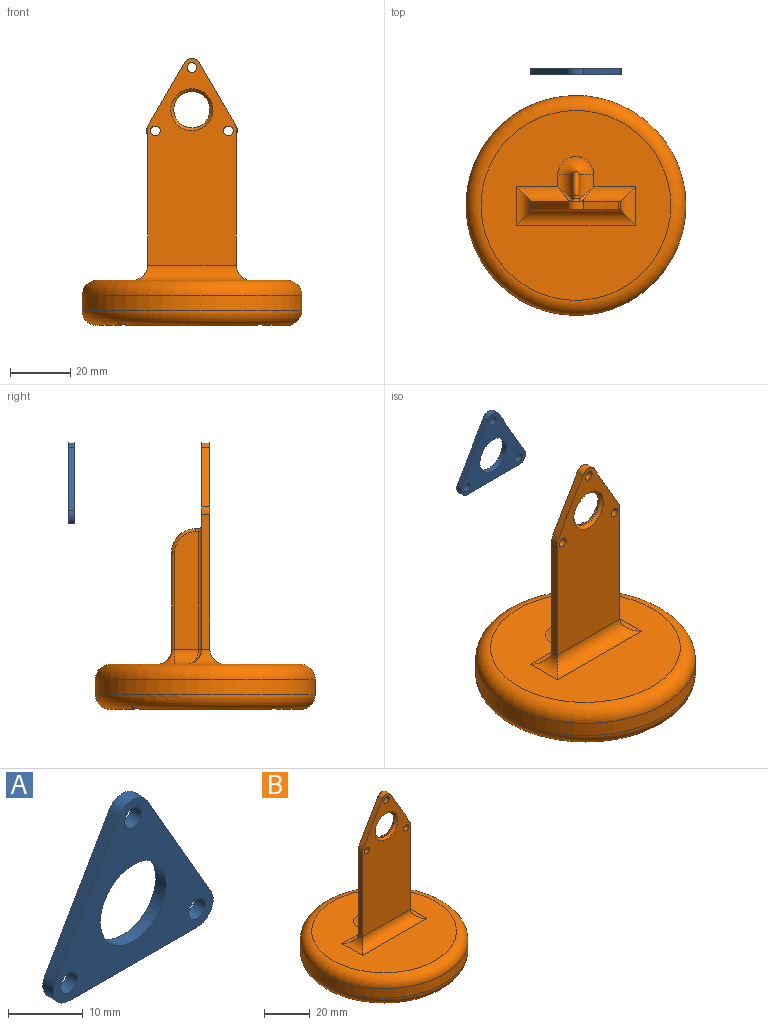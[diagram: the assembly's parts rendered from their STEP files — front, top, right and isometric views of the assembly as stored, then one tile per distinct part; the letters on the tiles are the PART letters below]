
ASSEMBLY  parts=2 mates=1
PART A: 12 faces, bbox 30.2x2x27 mm
  f0: cylinder r=3mm len=4.5mm, axis (0,1,0), area 12.6mm2, adj f1,f9,f10,f11
  f1: plane 21x12.12mm, normal (0.87,0,0.5), area 48.5mm2, adj f0,f2,f10,f11
  f2: cylinder r=3mm len=5.2mm, axis (0,1,0), area 12.6mm2, adj f1,f3,f10,f11
  f3: plane 21x12.12mm, normal (-0.87,0,0.5), area 48.5mm2, adj f2,f4,f10,f11
  f4: cylinder r=3mm len=4.5mm, axis (0,1,0), area 12.6mm2, adj f3,f9,f10,f11
  f5: cylinder r=1.6mm len=3.2mm, axis (0,1,0), area 20.1mm2, adj f10,f11
  f6: cylinder r=1.6mm len=3.2mm, axis (0,1,0), area 20.1mm2, adj f10,f11
  f7: cylinder r=1.6mm len=3.2mm, axis (0,1,0), area 20.1mm2, adj f10,f11
  f8: cylinder r=6.25mm len=12.5mm, axis (0,1,0), area 78.5mm2, adj f10,f11
  f9: plane 24.25x2mm, normal (0,0,-1), area 48.5mm2, adj f0,f4,f10,f11
  f10: plane 30.25x27mm, normal (0,-1,0), area 354.3mm2, adj f0,f1,f2,f3,f4,f5,f6,f7
  f11: plane 30.25x27mm, normal (0,1,0), area 354.3mm2, adj f0,f1,f2,f3,f4,f5,f6,f7
PART B: 62 faces, bbox 79x79x88.7 mm
  f0: plane 40.8x7.5mm, normal (0,0,-1), area 209.4mm2, adj f48,f54
  f1: plane 40.8x7.5mm, normal (0,0,-1), area 209.4mm2, adj f48,f51
  f2: plane 40.8x7.5mm, normal (0,0,-1), area 209.4mm2, adj f48,f57
  f3: plane 63x63mm, normal (0,0,1), area 2511.7mm2, adj f39,f40,f41,f42,f43,f44,f46,f47
  f4: plane 40.8x7.5mm, normal (0,0,-1), area 209.4mm2, adj f48,f60
  f5: cylinder r=36.5mm len=73mm, axis (0,0,-1), area 1146.7mm2, adj f48,f49
  f6: plane 46x11mm, normal (-1,0,0), area 505.3mm2, adj f7,f9,f10,f55,f57,f59
  f7: plane 46x11mm, normal (0,1,0), area 505.3mm2, adj f6,f8,f10,f58,f60,f61
  f8: plane 46x11mm, normal (1,0,0), area 505.3mm2, adj f7,f9,f10,f52,f54,f56
  f9: plane 46x11mm, normal (0,-1,0), area 505.3mm2, adj f6,f8,f10,f50,f51,f53
  f10: plane 46x46mm, normal (0,0,-1), area 2116mm2, adj f6,f7,f8,f9
  f11: plane 19.84x11.45mm, normal (-0.87,0,0.5), area 61.9mm2, adj f12,f20,f21,f22
  f12: cylinder r=5mm len=2.7mm, axis (0,1,0), area 7.1mm2, adj f11,f13,f21,f22
  f13: plane 44.75x2.7mm, normal (-1,0,0), area 120.8mm2, adj f12,f21,f22,f42
  f14: plane 44.75x2.7mm, normal (1,0,0), area 120.8mm2, adj f15,f21,f22,f46
  f15: cylinder r=5mm len=2.7mm, axis (0,1,0), area 7.1mm2, adj f14,f16,f21,f22
  f16: plane 19.84x11.45mm, normal (0.87,0,0.5), area 61.9mm2, adj f15,f20,f21,f22
  f17: cylinder r=1.6mm len=3.2mm, axis (0,1,0), area 27.1mm2, adj f21,f22
  f18: cylinder r=1.6mm len=3.2mm, axis (0,1,0), area 27.1mm2, adj f21,f22
  f19: cylinder r=1.6mm len=3.2mm, axis (0,1,0), area 27.1mm2, adj f21,f22
  f20: cylinder r=3mm len=5.2mm, axis (0,1,0), area 17mm2, adj f11,f16,f21,f22
  f21: plane 68.59x29.45mm, normal (0,-1,0), area 1548mm2, adj f11,f12,f13,f14,f15,f16,f17,f18
  f22: plane 68.59x29.45mm, normal (0,1,0), area 1381.6mm2, adj f11,f12,f13,f14,f15,f16,f17,f18
  f23: cylinder r=0.9mm len=1.8mm, axis (0,-1,0), area 3.3mm2, adj f22,f24,f26,f27
  f24: cylinder r=7.15mm len=14.19mm, axis (0,-1,0), area 24.8mm2, adj f22,f23,f25,f27
  f25: cylinder r=0.9mm len=1.8mm, axis (0,-1,0), area 3.3mm2, adj f22,f24,f26,f27
  f26: cylinder r=7.15mm len=14.19mm, axis (0,-1,0), area 24.8mm2, adj f22,f23,f25,f27
  f27: plane 14.3x14.19mm, normal (0,1,0), area 45mm2, adj f23,f24,f25,f26,f28
  f28: cylinder r=6mm len=12mm, axis (0,1,0), area 18.8mm2, adj f27,f29
  f29: cone r=7mm half-angle=45deg, axis (0,-1,0), area 57.8mm2, adj f21,f28
  f30: plane 39x8mm, normal (-1,0,0), area 301.5mm2, adj f32,f33,f34,f36,f39
  f31: plane 39x8mm, normal (1,0,0), area 301.5mm2, adj f32,f34,f36,f37,f43
  f32: cylinder r=1mm len=32mm, axis (0,0,-1), area 100.5mm2, adj f30,f31,f34,f41
  f33: cylinder r=1mm len=39mm, axis (0,0,-1), area 61.3mm2, adj f22,f30,f35,f38
  f34: torus R=7mm, axis (1,0,0), area 37.7mm2, adj f30,f31,f32,f36
  f35: torus R=2mm, axis (0,-1,0), area 6.7mm2, adj f22,f33,f36,f37
  f36: cylinder r=1mm len=2mm, axis (0,-1,0), area 3.1mm2, adj f30,f31,f34,f35
  f37: cylinder r=1mm len=39mm, axis (0,0,1), area 61.3mm2, adj f22,f31,f35,f45
  f38: bspline ~5.78x5mm, area 5.4mm2, adj f33,f39,f40
  f39: cylinder r=5mm len=8mm, axis (0,-1,0), area 47.1mm2, adj f3,f30,f38,f41
  f40: cylinder r=5mm len=17.72mm, axis (1,0,0), area 103.8mm2, adj f3,f22,f38,f42
  f41: torus R=6mm, axis (0,0,1), area 69.5mm2, adj f3,f32,f39,f43
  f42: cylinder r=5mm len=12.7mm, axis (0,1,0), area 60.5mm2, adj f3,f13,f40,f44
  f43: cylinder r=5mm len=8mm, axis (0,1,0), area 47.1mm2, adj f3,f31,f41,f45
  f44: cylinder r=5mm len=39.45mm, axis (-1,0,0), area 270.5mm2, adj f3,f21,f42,f46
  f45: bspline ~5.78x5mm, area 5.4mm2, adj f37,f43,f47
  f46: cylinder r=5mm len=12.7mm, axis (0,-1,0), area 60.5mm2, adj f3,f14,f44,f47
  f47: cylinder r=5mm len=17.72mm, axis (1,0,0), area 103.8mm2, adj f3,f22,f45,f46
  f48: torus R=31.5mm, axis (0,0,1), area 1677mm2, adj f0,f1,f2,f4,f5,f50,f52,f53
  f49: torus R=31.5mm, axis (0,0,1), area 1711.5mm2, adj f3,f5
  f50: bspline ~7.02x2.36mm, area 6.1mm2, adj f9,f48,f51,f52
  f51: cylinder r=1mm len=40.8mm, axis (1,0,0), area 64.1mm2, adj f1,f9,f50,f53
  f52: bspline ~7.02x2.36mm, area 6.1mm2, adj f8,f48,f50,f54
  f53: bspline ~5.79x2.36mm, area 6.1mm2, adj f9,f48,f51,f55
  f54: cylinder r=1mm len=40.8mm, axis (0,1,0), area 64.1mm2, adj f0,f8,f52,f56
  f55: bspline ~7.02x2.36mm, area 6.1mm2, adj f6,f48,f53,f57
  f56: bspline ~7.02x2.36mm, area 6.1mm2, adj f8,f48,f54,f58
  f57: cylinder r=1mm len=40.8mm, axis (0,-1,0), area 64.1mm2, adj f2,f6,f55,f59
  f58: bspline ~7.02x2.36mm, area 6.1mm2, adj f7,f48,f56,f60
  f59: bspline ~5.79x2.36mm, area 6.1mm2, adj f6,f48,f57,f61
  f60: cylinder r=1mm len=40.8mm, axis (-1,0,0), area 64.1mm2, adj f4,f7,f58,f61
  f61: bspline ~7.02x2.36mm, area 6.1mm2, adj f7,f48,f59,f60
PLACE A t=(-2.95,42,20.85)mm
PLACE B t=(-2.95,-3.28,-50.74)mm
MATE cylindrical A.f2 <-> B.f19  axis (0,1,0) through (-2.95,42,34.85)mm
